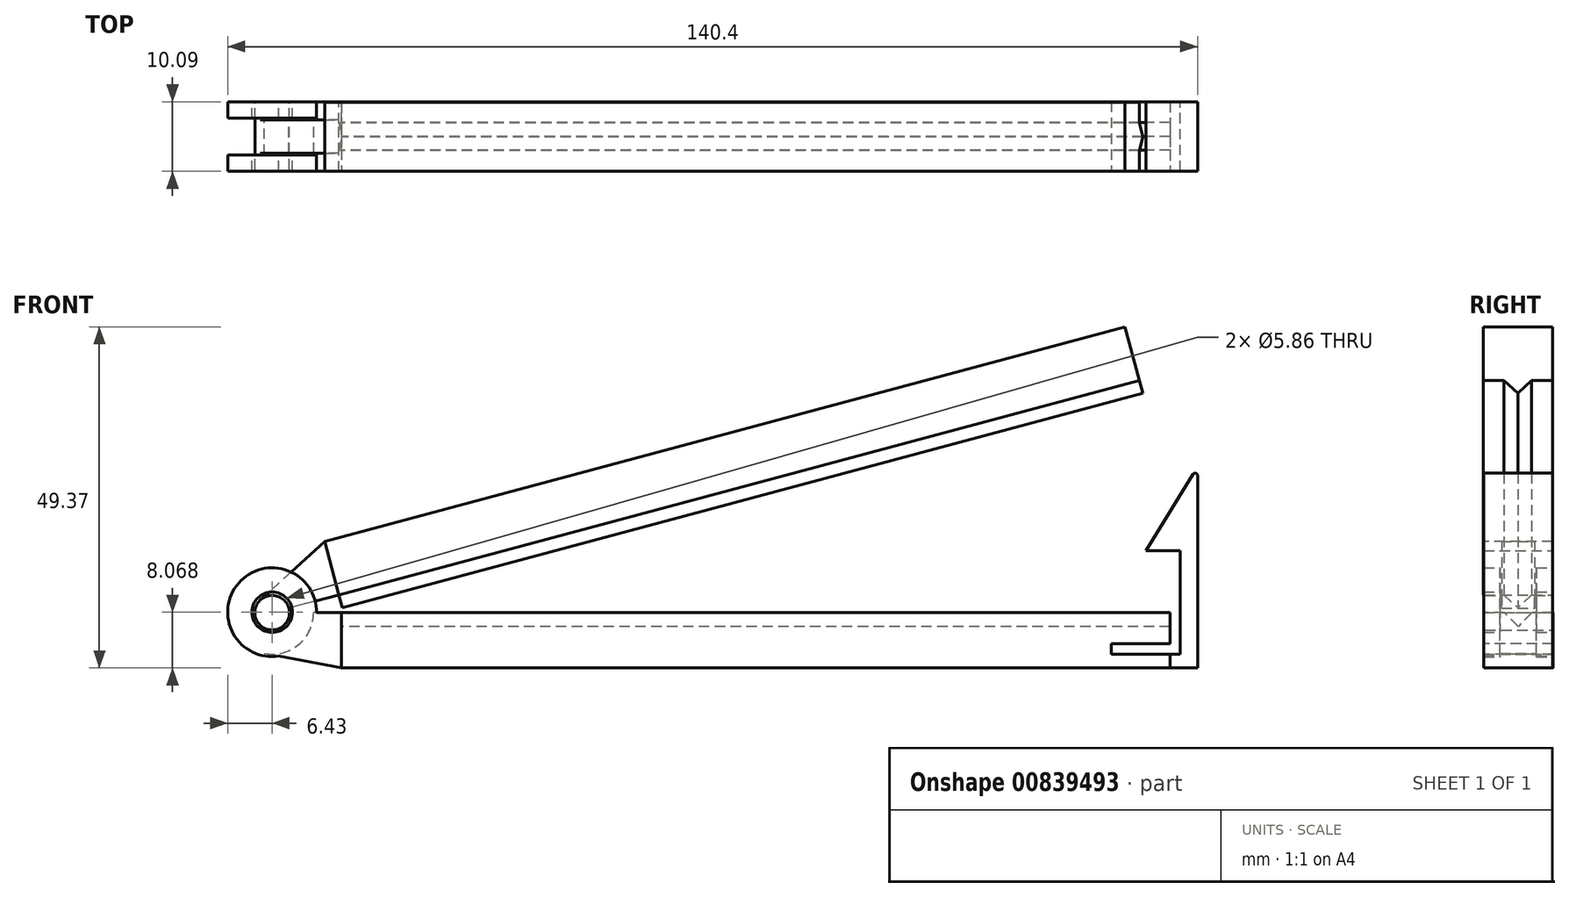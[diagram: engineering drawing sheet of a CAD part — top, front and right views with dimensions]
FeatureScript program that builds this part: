
annotation { "Feature Type Name" : "Feature", "Feature Type Description" : "" }
export const myFeature = defineFeature(function(context is Context, id is Id, definition is map)
    precondition{}
    {
        {
            assignVariable(context, id + "F0", {"name" : "len", "anyValue" : 1.33});
        }
        {
            var Q0;
            Q0=qCreatedBy(makeId("Front.planeOp"),FACE);
            var sketch = newSketch(context, id + "F1", { "sketchPlane" : qUnion([Q0])});
            skPoint(sketch, "E0.middle", {"position": v(0, 0) * mm});
            skCircle(sketch, "E1", {"center": v(0, -55) * mm, "radius": 2.5 * mm});
            skLineSegment(sketch, "E2", {"start": v(0, -45) * mm, "end": v(0, 74.97) * mm});
            skLineSegment(sketch, "E3", {"start": v(-8, 74.97) * mm, "end": v(0, 74.97) * mm});
            skLineSegment(sketch, "E4", {"start": v(-8, -45) * mm, "end": v(-8, 74.97) * mm});
            skLineSegment(sketch, "E5", {"start": v(-8, -45) * mm, "end": v(-2.22, -56.15) * mm});
            skLineSegment(sketch, "E6", {"start": v(0, -45) * mm, "end": v(0, -52.5) * mm});
            skLineSegment(sketch, "E7", {"start": v(-8, -45) * mm, "end": v(0, -45) * mm});
            skSolve(sketch);
        }
        {
            var Q0;
            Q0=qCreatedBy(makeId("Top.planeOp"),FACE);
            var sketch = newSketch(context, id + "F2", { "sketchPlane" : qUnion([Q0])});
            skPoint(sketch, "E8.middle", {"position": v(-4, -0.05) * mm});
            skPoint(sketch, "E9.middle", {"position": v(0, 0) * mm});
            skPoint(sketch, "E10", {"position": v(-2, 2.95) * mm});
            skLineSegment(sketch, "E11", {"start": v(-8, 4.95) * mm, "end": v(0, 4.95) * mm});
            skLineSegment(sketch, "E12", {"start": v(0, -5.05) * mm, "end": v(-8, -5.05) * mm});
            skLineSegment(sketch, "E13", {"start": v(-8, 4.95) * mm, "end": v(-8, -5.05) * mm});
            skLineSegment(sketch, "E14", {"start": v(-4, -17.2) * mm, "end": v(-4, 23.1) * mm, "construction": true});
            skPoint(sketch, "E14.endSnap0", {"position": v(-4, -5.05) * mm});
            skLineSegment(sketch, "E15", {"start": v(-11.5, -0.05) * mm, "end": v(7.57, -0.05) * mm, "construction": true});
            skLineSegment(sketch, "E16", {"start": v(7.57, -0.05) * mm, "end": v(7.57, -2.05) * mm, "construction": true});
            skLineSegment(sketch, "E17", {"start": v(7.57, -2.05) * mm, "end": v(0, -2.05) * mm, "construction": true});
            skLineSegment(sketch, "E18", {"start": v(-2, -2.05) * mm, "end": v(-2, 2) * mm, "construction": true});
            skLineSegment(sketch, "E19", {"start": v(0, -9.62) * mm, "end": v(0, 12.5) * mm, "construction": true});
            skLineSegment(sketch, "E20", {"start": v(0, -5.05) * mm, "end": v(0, -2.05) * mm});
            skLineSegment(sketch, "E21", {"start": v(0, 1.95) * mm, "end": v(0, 4.95) * mm});
            skLineSegment(sketch, "E22.MirrorCS", {"start": v(0, 1.95) * mm, "end": v(1.97, -0.05) * mm});
            skLineSegment(sketch, "E23.MirrorCS", {"start": v(0, -2.05) * mm, "end": v(1.97, -0.05) * mm});
            skSolve(sketch);
        }
        {
            var Q0;
            {var subQ0=sQuery(id+"F1.wireOp",EDGE,"E5");Q0=makeQuery(id+"F1.imprint","IMPRINT",FACE,{"disambiguationData":[TD([[makeQuery(id+"F1.imprint","IMPRINT",EDGE,{"derivedFrom":subQ0}),1.0]])]});}
            extrude(context, id + "F3", {"entities" : qUnion([Q0]), "depth" : 2.4 * mm, "offsetDistance" : 25 * mm, "hasSecondDirection" : true, "secondDirectionOppositeDirection" : true, "secondDirectionDepth" : 2.4 * mm});
        }
        {
            var Q0;
            Q0=makeQuery(id+"F2.imprint","IMPRINT",FACE,{"disambiguationData":[TD([[makeQuery(id+"F2.imprint","IMPRINT",EDGE,{"derivedFrom":sQuery(id+"F2.wireOp",EDGE,"E11")}),-1.0]])]});
            extrude(context, id + "F4", {"entities" : qUnion([Q0]), "depth" : ((getVariable(context, 'len') * 90) - 45) * mm, "offsetDistance" : 25 * mm, "hasSecondDirection" : true, "secondDirectionOppositeDirection" : true, "secondDirectionDepth" : 45 * mm});
        }
        {
            var Q0;
            {var subQ0=sQuery(id+"F1.wireOp",EDGE,"E1");var subQ1=makeQuery(id+"F1.imprint","INTERSECT",VERTEX,{"derivedFrom":[subQ0,sQuery(id+"F1.wireOp",EDGE,"y2ifkrbQ-fr0k-EV40-WAJp-tS3gvMkOgowK")]});Q0=makeQuery(id+"F1.imprint","IMPRINT",FACE,{"disambiguationData":[TD([[makeQuery(id+"F1.imprint","IMPRINT",EDGE,{"disambiguationData":[TD([[subQ1,1.0]])],"derivedFrom":subQ0}),1.0]])]});}
            extrude(context, id + "F5", {"entities" : qUnion([Q0]), "operationType" : NewBodyOperationType.ADD, "depth" : 5 * mm, "offsetDistance" : 25 * mm, "hasSecondDirection" : true, "secondDirectionOppositeDirection" : true, "secondDirectionDepth" : 5 * mm});
        }
        {
            var Q0;
            Q0=makeQuery(id+"F5.opExtrude","CAP_EDGE",EDGE,{"disambiguationData":[OSD([sQuery(id+"F1.wireOp",EDGE,"E1")])],"isStart":false});
            var Q1;
            Q1=makeQuery(id+"F5.opExtrude","CAP_EDGE",EDGE,{"disambiguationData":[OSD([sQuery(id+"F1.wireOp",EDGE,"E1")])],"isStart":true});
            fillet(context, id + "F6", {"entities" : qUnion([Q0, Q1]), "radius" : .25 * mm, "tangentPropagation" : true, "allowEdgeOverflow" : false});
        }
        {
            var Q0;
            Q0=makeQuery(id+"F4.opExtrude","SWEPT_FACE",FACE,{"disambiguationData":[OSD([sQuery(id+"F2.wireOp",EDGE,"ip5yjFWY-FGmT-liJ9-8fW3-jcPs83EoBgNt")])]});
            var Q1;
            Q1=qCreatedBy(makeId("Front.planeOp"),FACE);
            cPlane(context, id + "F7", {"entities" : qUnion([Q0, Q1]), "cplaneType" : CPlaneType.OFFSET, "offset" : 0 * mm, "width" : 150 * mm, "height" : 150 * mm});
        }
        {
            var Q0;
            Q0=qCreatedBy(id+"F7.planeOp",FACE);
            var sketch = newSketch(context, id + "F8", { "sketchPlane" : qUnion([Q0])});
            skLineSegment(sketch, "E24", {"start": v(0, -48.5) * mm, "end": v(0, -47.5) * mm});
            skLineSegment(sketch, "E25.right", {"start": v(10, -55) * mm, "end": v(10, -63) * mm});
            skLineSegment(sketch, "E26", {"start": v(0, -52.02) * mm, "end": v(0, -52.5) * mm});
            skLineSegment(sketch, "E27", {"start": v(10, -63) * mm, "end": v(129.97, -63) * mm});
            skLineSegment(sketch, "E28", {"start": v(10, -55) * mm, "end": v(129.97, -55) * mm});
            skLineSegment(sketch, "E29", {"start": v(10, -55) * mm, "end": v(10, -32.35) * mm, "construction": true});
            skLineSegment(sketch, "E30", {"start": v(0, -52.5) * mm, "end": v(0, -53.04) * mm});
            skPoint(sketch, "E31.visualSharp", {"position": v(0, -53.37) * mm});
            skLineSegment(sketch, "E32", {"start": v(129.97, -55) * mm, "end": v(129.97, -63) * mm});
            skLineSegment(sketch, "E33", {"start": v(0, -62.82) * mm, "end": v(0, -45.65) * mm, "construction": true});
            skLineSegment(sketch, "E34", {"start": v(1.79, -54.77) * mm, "end": v(1.79, -55) * mm, "construction": true});
            skPoint(sketch, "E35", {"position": v(0, -55) * mm});
            skLineSegment(sketch, "E36", {"start": v(-10.98, -55) * mm, "end": v(16.63, -55) * mm, "construction": true});
            skCircle(sketch, "E37", {"center": v(0, -55) * mm, "radius": 3 * mm, "construction": true});
            skCircle(sketch, "E38", {"center": v(0, -55) * mm, "radius": 6 * mm, "construction": true});
            skLineSegment(sketch, "E39", {"start": v(10, -63) * mm, "end": v(-1.12, -60.9) * mm});
            skLineSegment(sketch, "E40", {"start": v(10, -55) * mm, "end": v(6, -55) * mm});
            skArc(sketch, "E41", {"start": v(6, -55) * mm, "mid": v(3.83, -59.62) * mm, "end": v(-1.12, -60.9) * mm});
            skCircle(sketch, "E42", {"center": v(0, -55) * mm, "radius": 129.97 * mm, "construction": true});
            skLineSegment(sketch, "E43", {"start": v(129.97, -63) * mm, "end": v(133.97, -63) * mm});
            skLineSegment(sketch, "E44", {"start": v(133.97, -63) * mm, "end": v(133.97, -35.18) * mm});
            skLineSegment(sketch, "E45", {"start": v(129.97, -55) * mm, "end": v(131.47, -55) * mm});
            skLineSegment(sketch, "E46", {"start": v(129.97, -59.5) * mm, "end": v(121.47, -59.5) * mm});
            skLineSegment(sketch, "E47", {"start": v(121.47, -59.5) * mm, "end": v(121.47, -61) * mm});
            skLineSegment(sketch, "E48", {"start": v(121.47, -61) * mm, "end": v(131.47, -61) * mm});
            skLineSegment(sketch, "E49", {"start": v(129.97, -55) * mm, "end": v(129.97, -59.5) * mm});
            skLineSegment(sketch, "E50", {"start": v(131.47, -61) * mm, "end": v(131.47, -55) * mm});
            skLineSegment(sketch, "E51", {"start": v(131.47, -55) * mm, "end": v(131.47, -46) * mm});
            skLineSegment(sketch, "E52", {"start": v(131.47, -46) * mm, "end": v(126.47, -46) * mm});
            skLineSegment(sketch, "E53", {"start": v(126.47, -46) * mm, "end": v(133.29, -34.99) * mm});
            skPoint(sketch, "E54.visualSharp", {"position": v(133.97, -33.89) * mm});
            skArc(sketch, "E54.filletArc", {"start": v(133.97, -35.18) * mm, "mid": v(133.7, -34.83) * mm, "end": v(133.29, -34.99) * mm});
            skSolve(sketch);
        }
        {
            var Q0;
            Q0=makeQuery(id+"F8.imprint","IMPRINT",FACE,{"disambiguationData":[TD([[makeQuery(id+"F8.imprint","IMPRINT",EDGE,{"derivedFrom":sQuery(id+"F8.wireOp",EDGE,"E25.right")}),-1.0]])]});
            extrude(context, id + "F9", {"entities" : qUnion([Q0]), "depth" : 5 * mm, "offsetDistance" : 25 * mm, "hasSecondDirection" : true, "secondDirectionOppositeDirection" : true, "secondDirectionDepth" : 5 * mm});
        }
        {
            var Q0;
            Q0=makeQuery(id+"F9.opExtrude","SWEPT_FACE",FACE,{"disambiguationData":[OSD([sQuery(id+"F8.wireOp",EDGE,"E25.right")])]});
            cPlane(context, id + "F10", {"entities" : qUnion([Q0]), "cplaneType" : CPlaneType.OFFSET, "offset" : 0 * mm, "width" : 150 * mm, "height" : 150 * mm});
        }
        {
            var Q0;
            Q0=qCreatedBy(id+"F10.planeOp",FACE);
            var sketch = newSketch(context, id + "F11", { "sketchPlane" : qUnion([Q0])});
            skPoint(sketch, "E55", {"position": v(0, -52.5) * mm});
            skLineSegment(sketch, "E56", {"start": v(0, -55) * mm, "end": v(0, -48.4) * mm, "construction": true});
            skPoint(sketch, "E57", {"position": v(-5, -55) * mm});
            skPoint(sketch, "E58", {"position": v(5.04, -54.96) * mm});
            skLineSegment(sketch, "E59", {"start": v(2.73, -55) * mm, "end": v(2.73, -57) * mm, "construction": true});
            skLineSegment(sketch, "E60", {"start": v(5.04, -54.96) * mm, "end": v(5.04, -63) * mm});
            skLineSegment(sketch, "E61", {"start": v(5.04, -63) * mm, "end": v(-4.96, -63) * mm});
            skLineSegment(sketch, "E62", {"start": v(-4.96, -63) * mm, "end": v(-5, -55) * mm});
            skLineSegment(sketch, "E63", {"start": v(5.04, -54.96) * mm, "end": v(2, -54.96) * mm});
            skLineSegment(sketch, "E64", {"start": v(2, -54.96) * mm, "end": v(0, -57) * mm});
            skLineSegment(sketch, "E65", {"start": v(0, -57) * mm, "end": v(-2, -55) * mm});
            skLineSegment(sketch, "E66", {"start": v(-2, -55) * mm, "end": v(-5, -55) * mm});
            skSolve(sketch);
        }
        {
            var Q0;
            Q0=makeQuery(id+"F3.opExtrude","SWEPT_FACE",FACE,{"disambiguationData":[OSD([sQuery(id+"F1.wireOp",EDGE,"E6")])]});
            cPlane(context, id + "F12", {"entities" : qUnion([Q0]), "cplaneType" : CPlaneType.OFFSET, "offset" : 0 * mm, "width" : 150 * mm, "height" : 150 * mm});
        }
        {
            var Q0;
            Q0=qCreatedBy(id+"F12.planeOp",FACE);
            var sketch = newSketch(context, id + "F13", { "sketchPlane" : qUnion([Q0])});
            skLineSegment(sketch, "E67", {"start": v(0.04, -49.4) * mm, "end": v(0.04, -62.56) * mm, "construction": true});
            skPoint(sketch, "E68", {"position": v(-5, -52) * mm});
            skLineSegment(sketch, "E69", {"start": v(-2.65, -52) * mm, "end": v(-5, -52) * mm});
            skLineSegment(sketch, "E70", {"start": v(-5, -52) * mm, "end": v(-5, -48.5) * mm});
            skLineSegment(sketch, "E71", {"start": v(-5, -48.5) * mm, "end": v(-2.65, -48.5) * mm});
            skLineSegment(sketch, "E72", {"start": v(-2.65, -48.5) * mm, "end": v(-2.65, -52) * mm});
            skLineSegment(sketch, "E73.MirrorCS", {"start": v(2.65, -48.5) * mm, "end": v(2.65, -52) * mm});
            skLineSegment(sketch, "E74.MirrorCS", {"start": v(5, -48.5) * mm, "end": v(2.65, -48.5) * mm});
            skLineSegment(sketch, "E75.MirrorCS", {"start": v(5, -52) * mm, "end": v(5, -48.5) * mm});
            skLineSegment(sketch, "E76.MirrorCS", {"start": v(2.65, -52) * mm, "end": v(5, -52) * mm});
            skLineSegment(sketch, "E77", {"start": v(5.85, -54.93) * mm, "end": v(-5.83, -54.93) * mm, "construction": true});
            skLineSegment(sketch, "E78", {"start": v(-1.72, -52.5) * mm, "end": v(-8.9, -52.5) * mm, "construction": true});
            skLineSegment(sketch, "E79", {"start": v(-8.9, -52.5) * mm, "end": v(9.2, -52.5) * mm, "construction": true});
            skSolve(sketch);
        }
        {
            var Q0;
            Q0=makeQuery(id+"F13.imprint","IMPRINT",FACE,{"disambiguationData":[TD([[makeQuery(id+"F13.imprint","IMPRINT",EDGE,{"derivedFrom":sQuery(id+"F13.wireOp",EDGE,"E69")}),-1.0]])]});
            var Q1;
            Q1=makeQuery(id+"F13.imprint","IMPRINT",FACE,{"disambiguationData":[TD([[makeQuery(id+"F13.imprint","IMPRINT",EDGE,{"derivedFrom":sQuery(id+"F13.wireOp",EDGE,"E73.MirrorCS")}),1.0]])]});
            var Q2;
            Q2=sQuery(id+"F13.wireOp",EDGE,"E77");
            revolve(context, id + "F14", {"operationType" : NewBodyOperationType.ADD, "surfaceOperationType" : NewSurfaceOperationType.NEW, "entities" : qUnion([Q0, Q1]), "axis" : qUnion([Q2]), "revolveType" : RevolveType.FULL});
        }
        {
            var Q0;
            Q0=makeQuery(id+"F11.imprint","IMPRINT",FACE,{"disambiguationData":[TD([[makeQuery(id+"F11.imprint","IMPRINT",EDGE,{"derivedFrom":sQuery(id+"F11.wireOp",EDGE,"E60")}),-1.0]])]});
            extrude(context, id + "F15", {"entities" : qUnion([Q0]), "operationType" : NewBodyOperationType.ADD, "depth" : (getVariable(context, 'len') * 90) * mm, "offsetDistance" : 25 * mm});
        }
        {
            var Q0;
            {var subQ0=sQuery(id+"F8.wireOp",EDGE,"E45");Q0=makeQuery(id+"F8.imprint","IMPRINT",FACE,{"disambiguationData":[TD([[makeQuery(id+"F8.imprint","IMPRINT",EDGE,{"derivedFrom":subQ0}),-1.0]])]});}
            var Q1;
            {var subQ3=sQuery(id+"F8.wireOp",EDGE,"E46");Q1=makeQuery(id+"F8.imprint","IMPRINT",FACE,{"disambiguationData":[TD([[makeQuery(id+"F8.imprint","IMPRINT",EDGE,{"derivedFrom":subQ3}),1.0]])]});}
            extrude(context, id + "F16", {"entities" : qUnion([Q0, Q1]), "operationType" : NewBodyOperationType.REMOVE, "oppositeDirection" : true, "depth" : 6 * mm, "offsetDistance" : 25 * mm, "hasSecondDirection" : true, "secondDirectionOppositeDirection" : false, "secondDirectionDepth" : 6 * mm});
        }
        {
            var Q0;
            {var subQ4=sQuery(id+"F8.wireOp",EDGE,"E43");Q0=makeQuery(id+"F8.imprint","IMPRINT",FACE,{"disambiguationData":[TD([[makeQuery(id+"F8.imprint","IMPRINT",EDGE,{"derivedFrom":subQ4}),1.0]])]});}
            extrude(context, id + "F17", {"entities" : qUnion([Q0]), "operationType" : NewBodyOperationType.ADD, "depth" : 5 * mm, "offsetDistance" : 25 * mm, "hasSecondDirection" : true, "secondDirectionOppositeDirection" : true, "secondDirectionDepth" : 5 * mm});
        }
        {
            var Q0;
            Q0=makeQuery(id+"F4.opExtrude","SWEPT_BODY",BODY,{"disambiguationData":[OSD([sQuery(id+"F2.wireOp",EDGE,"E11"),sQuery(id+"F2.wireOp",EDGE,"d17a5c41-abb0-4a06-87f9-240cfe76f536"),sQuery(id+"F2.wireOp",EDGE,"86415b01-d5d1-4444-964a-f8bcd33acb26"),sQuery(id+"F2.wireOp",EDGE,"fe888662-1e42-41e0-a4d1-9fcc9647f306"),sQuery(id+"F2.wireOp",EDGE,"99ef5239-a491-45ab-b78d-13a00018c3ed"),sQuery(id+"F2.wireOp",EDGE,"E12"),sQuery(id+"F2.wireOp",EDGE,"E13")])]});
            var Q1;
            Q1=makeQuery(id+"F3.opExtrude","SWEPT_BODY",BODY,{"disambiguationData":[OSD([sQuery(id+"F1.wireOp",EDGE,"E1"),sQuery(id+"F1.wireOp",EDGE,"E5"),sQuery(id+"F1.wireOp",EDGE,"E6"),sQuery(id+"F1.wireOp",EDGE,"E7")])]});
            var Q2;
            Q2=makeQuery(id+"F5.opExtrude","SWEPT_BODY",BODY,{"disambiguationData":[OSD([sQuery(id+"F1.wireOp",EDGE,"E1")])]});
            var Q3;
            {var subQ0=sQuery(id+"F1.wireOp",EDGE,"E1");Q3=makeQuery(id+"F6.opFillet","BLEND_EDGE",EDGE,{"blendedFrom":[makeQuery(id+"F5.opExtrude","CAP_EDGE",EDGE,{"disambiguationData":[OSD([subQ0])],"isStart":false}),makeQuery(id+"F5.opExtrude","CAP_FACE",FACE,{"disambiguationData":[OSD([subQ0])],"isStart":false})],"blendedInto":[makeQuery(id+"F5.opExtrude","CAP_FACE",FACE,{"disambiguationData":[OSD([subQ0])],"isStart":false})]});}
            transform(context, id + "F18", {"entities" : qUnion([Q0, Q1, Q2]), "transformType" : TransformType.ROTATION, "transformAxis" : qUnion([Q3]), "angle" : 75 * degree, "oppositeDirection" : true, "makeCopy" : false});
        }
    });
